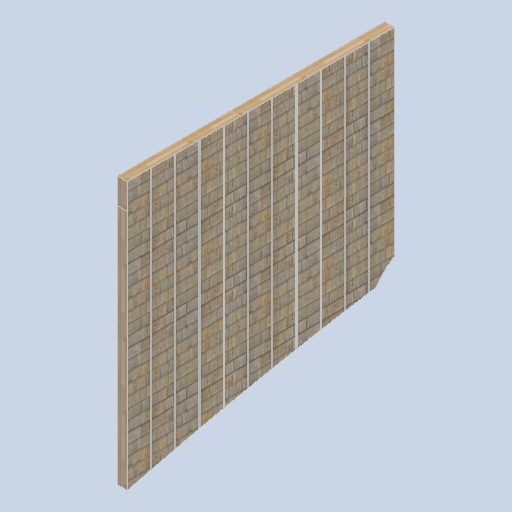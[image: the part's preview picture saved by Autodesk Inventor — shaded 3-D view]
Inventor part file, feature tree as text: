
AUTODESK INVENTOR PART (.ipt)
format: ipt  version: 2024.2 (Build 282272000, 272)  size: 329,216 bytes
history: native  units: in
note: dims shown in document units (in); Inventor stores cm internally (conversion verified against a paired STEP export)
features: other x3, sketch x2
ambient origin geometry x8: Origin, YZ Plane, XZ Plane, XY Plane, X Axis, Y Axis, Z Axis, Center Point
bodies: Solid1 (feature_tree)
feature tree (5):
  other  "side_wall_01.ipt"
  other  "Solid1::side_wall_01.ipt"
  other  "TaggingFeature1"
  sketch  "Sketch1"  dims[d0=0.3937in]
  sketch  "Sketch2"
